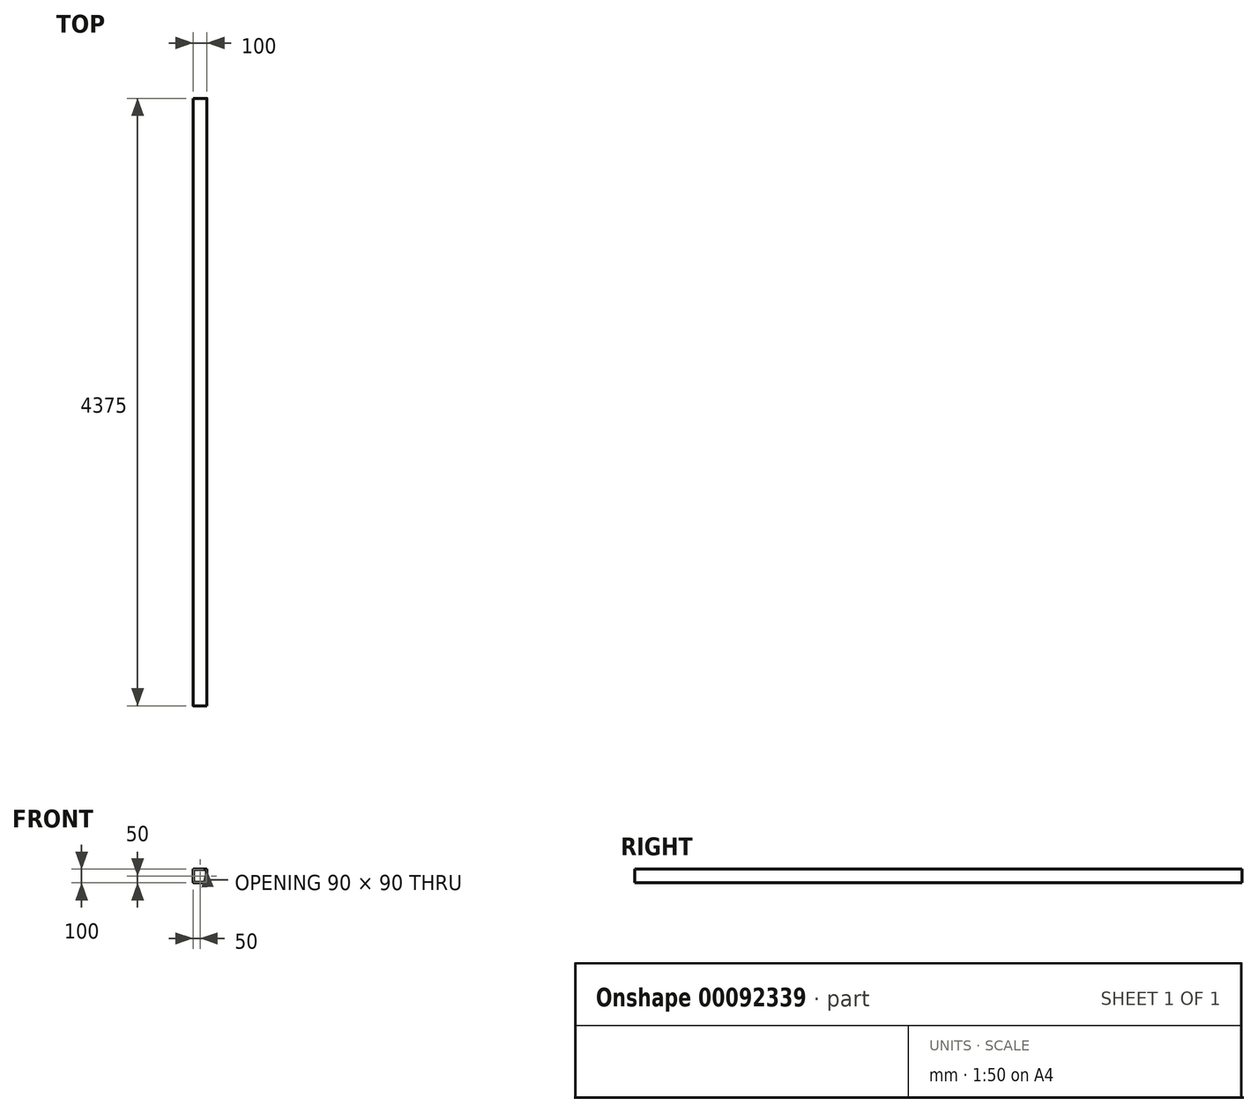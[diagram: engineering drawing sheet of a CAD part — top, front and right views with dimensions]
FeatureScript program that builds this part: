
annotation { "Feature Type Name" : "Feature", "Feature Type Description" : "" }
export const myFeature = defineFeature(function(context is Context, id is Id, definition is map)
    precondition{}
    {
        {
            var Q0;
            Q0=qCreatedBy(makeId("Front.planeOp"),FACE);
            var sketch = newSketch(context, id + "F0", { "sketchPlane" : qUnion([Q0])});
            skLineSegment(sketch, "E0.bottom", {"start": v(5, 0) * mm, "end": v(95, 0) * mm});
            skLineSegment(sketch, "E0.top", {"start": v(5, 100) * mm, "end": v(95, 100) * mm});
            skLineSegment(sketch, "E0.left", {"start": v(0, 5) * mm, "end": v(0, 95) * mm});
            skLineSegment(sketch, "E0.right", {"start": v(100, 5) * mm, "end": v(100, 95) * mm});
            skPoint(sketch, "E1.visualSharp", {"position": v(0, 100) * mm});
            skArc(sketch, "E1.filletArc", {"start": v(5, 100) * mm, "mid": v(1.46, 98.54) * mm, "end": v(0, 95) * mm});
            skPoint(sketch, "E2.visualSharp", {"position": v(100, 100) * mm});
            skArc(sketch, "E2.filletArc", {"start": v(100, 95) * mm, "mid": v(98.54, 98.54) * mm, "end": v(95, 100) * mm});
            skPoint(sketch, "E3.visualSharp", {"position": v(100, 0) * mm});
            skArc(sketch, "E3.filletArc", {"start": v(95, 0) * mm, "mid": v(98.54, 1.46) * mm, "end": v(100, 5) * mm});
            skPoint(sketch, "E4.visualSharp", {"position": v(0, 0) * mm});
            skArc(sketch, "E4.filletArc", {"start": v(0, 5) * mm, "mid": v(1.46, 1.46) * mm, "end": v(5, 0) * mm});
            skLineSegment(sketch, "E5.0", {"start": v(10, 95) * mm, "end": v(90, 95) * mm});
            skLineSegment(sketch, "E6.0", {"start": v(95, 10) * mm, "end": v(95, 90) * mm});
            skLineSegment(sketch, "E7.0", {"start": v(10, 5) * mm, "end": v(90, 5) * mm});
            skLineSegment(sketch, "E8.0", {"start": v(5, 10) * mm, "end": v(5, 90) * mm});
            skArc(sketch, "E9.filletArc", {"start": v(10, 95) * mm, "mid": v(6.46, 93.54) * mm, "end": v(5, 90) * mm});
            skArc(sketch, "E10.filletArc", {"start": v(5, 10) * mm, "mid": v(6.46, 6.46) * mm, "end": v(10, 5) * mm});
            skArc(sketch, "E11.filletArc", {"start": v(90, 5) * mm, "mid": v(93.54, 6.46) * mm, "end": v(95, 10) * mm});
            skArc(sketch, "E12.filletArc", {"start": v(95, 90) * mm, "mid": v(93.54, 93.54) * mm, "end": v(90, 95) * mm});
            skSolve(sketch);
        }
        {
            var Q0;
            Q0 = qSketchRegion(id + "F0", true);
            extrude(context, id + "F1", {"entities" : qUnion([Q0]), "depth" : 4375 * mm, "offsetDistance" : 25 * mm});
        }
    });
